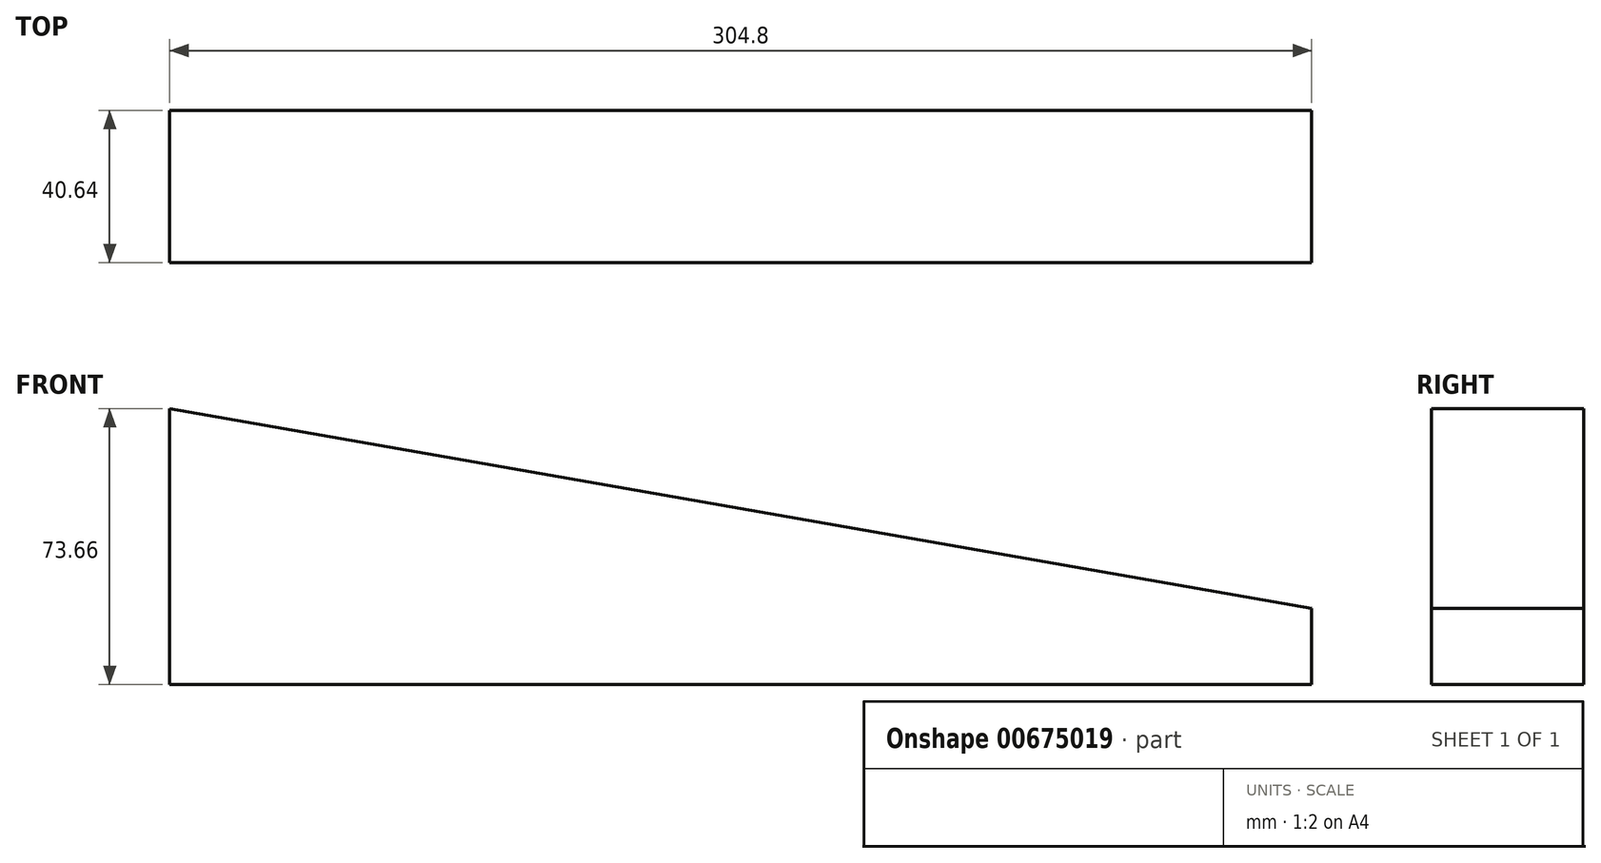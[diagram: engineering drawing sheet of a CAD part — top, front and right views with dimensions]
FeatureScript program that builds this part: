
annotation { "Feature Type Name" : "Feature", "Feature Type Description" : "" }
export const myFeature = defineFeature(function(context is Context, id is Id, definition is map)
    precondition{}
    {
        {
            var Q0;
            Q0=qCreatedBy(makeId("Front.planeOp"),FACE);
            var sketch = newSketch(context, id + "F0", { "sketchPlane" : qUnion([Q0])});
            skLineSegment(sketch, "E0", {"start": v(0, 0) * mm, "end": v(0, 73.66) * mm});
            skLineSegment(sketch, "E1", {"start": v(0, 73.66) * mm, "end": v(304.8, 20.32) * mm});
            skLineSegment(sketch, "E2", {"start": v(304.8, 20.32) * mm, "end": v(304.8, 0) * mm});
            skLineSegment(sketch, "E3", {"start": v(304.8, 0) * mm, "end": v(0, 0) * mm});
            skSolve(sketch);
        }
        {
            var Q0;
            Q0=makeQuery(id+"F0.imprint","IMPRINT",FACE,{"disambiguationData":[TD([[makeQuery(id+"F0.imprint","IMPRINT",EDGE,{"derivedFrom":sQuery(id+"F0.wireOp",EDGE,"E0")}),-1.0]])]});
            extrude(context, id + "F1", {"entities" : qUnion([Q0]), "depth" : 40.64 * mm, "offsetDistance" : 25.4 * mm});
        }
    });
